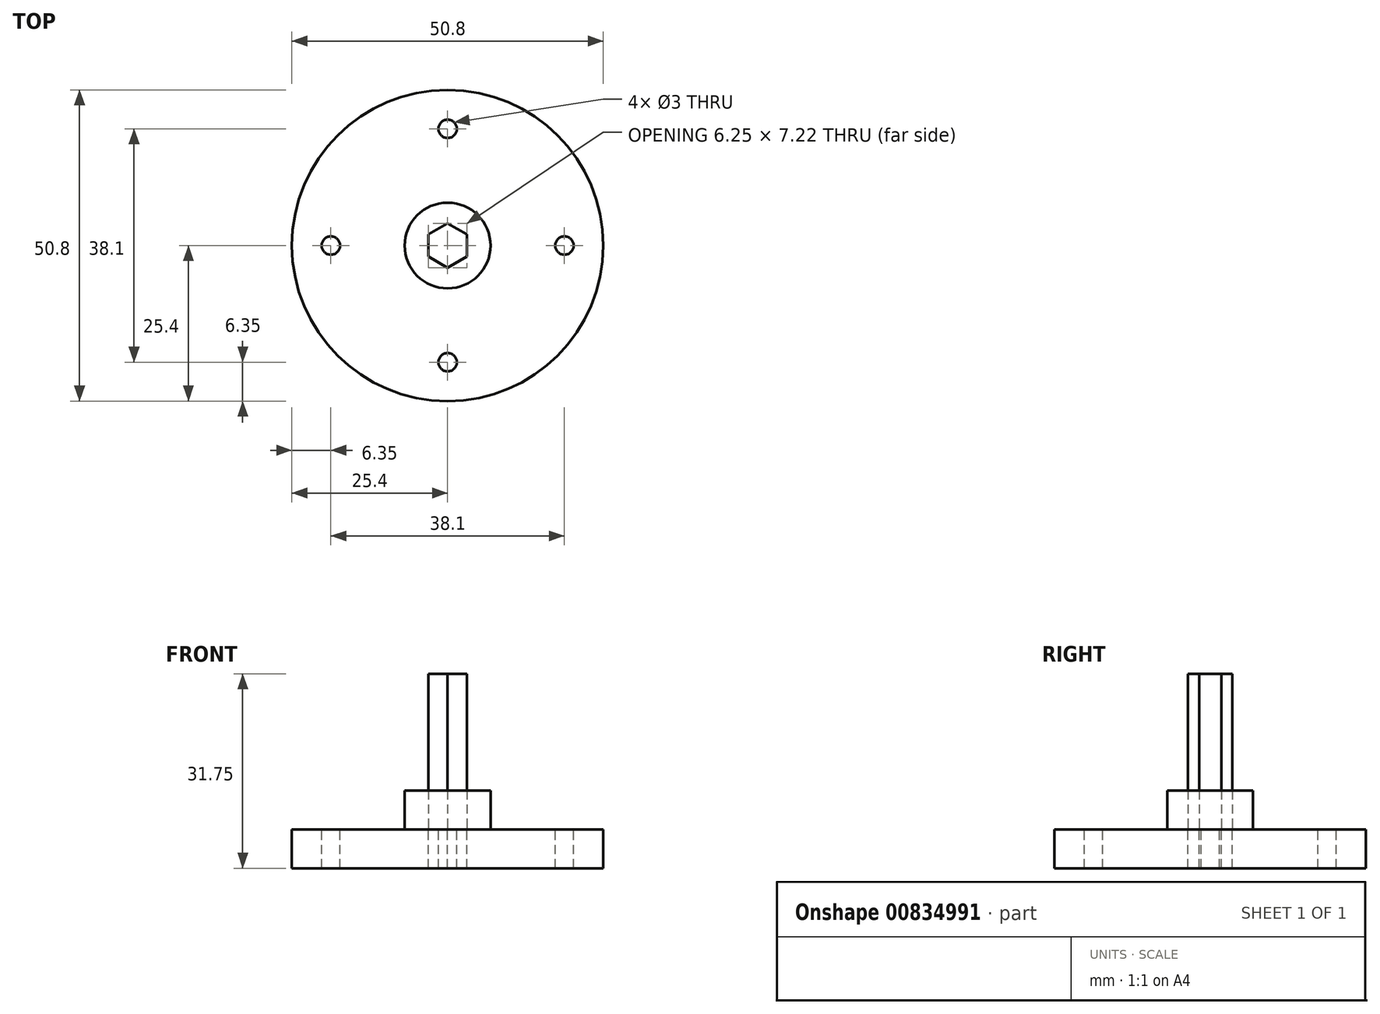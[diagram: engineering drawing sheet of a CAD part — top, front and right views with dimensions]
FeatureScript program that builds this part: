
annotation { "Feature Type Name" : "Feature", "Feature Type Description" : "" }
export const myFeature = defineFeature(function(context is Context, id is Id, definition is map)
    precondition{}
    {
        {
            var Q0;
            Q0=qCreatedBy(makeId("Top.planeOp"),FACE);
            var sketch = newSketch(context, id + "F0", { "sketchPlane" : qUnion([Q0])});
            skCircle(sketch, "E0.cCircle", {"center": v(0, 0) * mm, "radius": 3.13 * mm, "construction": true});
            skLineSegment(sketch, "E0.0", {"start": v(3.13, 1.8) * mm, "end": v(3.13, -1.8) * mm});
            skLineSegment(sketch, "E0.1", {"start": v(3.12, -1.8) * mm, "end": v(0, -3.6) * mm});
            skLineSegment(sketch, "E0.2", {"start": v(0, -3.6) * mm, "end": v(-3.12, -1.8) * mm});
            skLineSegment(sketch, "E0.3", {"start": v(-3.12, -1.8) * mm, "end": v(-3.13, 1.8) * mm});
            skLineSegment(sketch, "E0.4", {"start": v(-3.13, 1.8) * mm, "end": v(0, 3.6) * mm});
            skLineSegment(sketch, "E0.5", {"start": v(0, 3.6) * mm, "end": v(3.13, 1.8) * mm});
            skPoint(sketch, "E0.0.midPoint", {"position": v(3.13, 0) * mm});
            skSolve(sketch);
        }
        {
            var Q0;
            Q0 = qSketchRegion(id + "F0", true);
            extrude(context, id + "F1", {"entities" : qUnion([Q0]), "depth" : 25.4 * mm, "offsetDistance" : 25.4 * mm});
        }
        {
            var Q0;
            Q0=makeQuery(id+"F1.opExtrude","CAP_FACE",FACE,{"disambiguationData":[OSD([sQuery(id+"F0.wireOp",EDGE,"E0.0"),sQuery(id+"F0.wireOp",EDGE,"E0.1"),sQuery(id+"F0.wireOp",EDGE,"E0.2"),sQuery(id+"F0.wireOp",EDGE,"E0.3"),sQuery(id+"F0.wireOp",EDGE,"E0.4"),sQuery(id+"F0.wireOp",EDGE,"E0.5")])],"isStart":true});
            var sketch = newSketch(context, id + "F2", { "sketchPlane" : qUnion([Q0])});
            skCircle(sketch, "E1", {"center": v(0, 0) * mm, "radius": 25.4 * mm});
            skSolve(sketch);
        }
        {
            var Q0;
            Q0=makeQuery(id+"F2.imprint","IMPRINT",FACE,{"disambiguationData":[TD([[makeQuery(id+"F2.imprint","IMPRINT",EDGE,{"derivedFrom":sQuery(id+"F2.wireOp",EDGE,"E1")}),1.0]])]});
            extrude(context, id + "F3", {"entities" : qUnion([Q0]), "depth" : 6.35 * mm, "offsetDistance" : 25.4 * mm});
        }
        {
            var Q0;
            Q0=makeQuery(id+"F3.opExtrude","CAP_FACE",FACE,{"disambiguationData":[OSD([sQuery(id+"F0.wireOp",EDGE,"E0.0"),sQuery(id+"F0.wireOp",EDGE,"E0.1"),sQuery(id+"F0.wireOp",EDGE,"E0.2"),sQuery(id+"F0.wireOp",EDGE,"E0.3"),sQuery(id+"F0.wireOp",EDGE,"E0.4"),sQuery(id+"F0.wireOp",EDGE,"E0.5"),sQuery(id+"F2.wireOp",EDGE,"E1")])],"isStart":true});
            var sketch = newSketch(context, id + "F4", { "sketchPlane" : qUnion([Q0])});
            skCircle(sketch, "E2", {"center": v(0, 0) * mm, "radius": 7 * mm});
            skSolve(sketch);
        }
        {
            var Q0;
            Q0 = qSketchRegion(id + "F4", true);
            extrude(context, id + "F5", {"entities" : qUnion([Q0]), "depth" : 6.35 * mm, "offsetDistance" : 25.4 * mm});
        }
        {
            var Q0;
            Q0=makeQuery(id+"F3.opExtrude","CAP_FACE",FACE,{"disambiguationData":[OSD([sQuery(id+"F0.wireOp",EDGE,"E0.0"),sQuery(id+"F0.wireOp",EDGE,"E0.1"),sQuery(id+"F0.wireOp",EDGE,"E0.2"),sQuery(id+"F0.wireOp",EDGE,"E0.3"),sQuery(id+"F0.wireOp",EDGE,"E0.4"),sQuery(id+"F0.wireOp",EDGE,"E0.5"),sQuery(id+"F2.wireOp",EDGE,"E1")])],"isStart":true});
            var sketch = newSketch(context, id + "F6", { "sketchPlane" : qUnion([Q0])});
            skCircle(sketch, "E3", {"center": v(0, 19.05) * mm, "radius": 1.5 * mm});
            skCircle(sketch, "E4", {"center": v(19.05, 0) * mm, "radius": 1.5 * mm});
            skCircle(sketch, "E5", {"center": v(0, -19.05) * mm, "radius": 1.5 * mm});
            skCircle(sketch, "E6", {"center": v(-19.05, 0) * mm, "radius": 1.5 * mm});
            skSolve(sketch);
        }
        {
            var Q0;
            Q0 = qSketchRegion(id + "F6", true);
            extrude(context, id + "F7", {"entities" : qUnion([Q0]), "operationType" : NewBodyOperationType.REMOVE, "oppositeDirection" : true, "depth" : 25.4 * mm, "offsetDistance" : 25.4 * mm});
        }
    });
